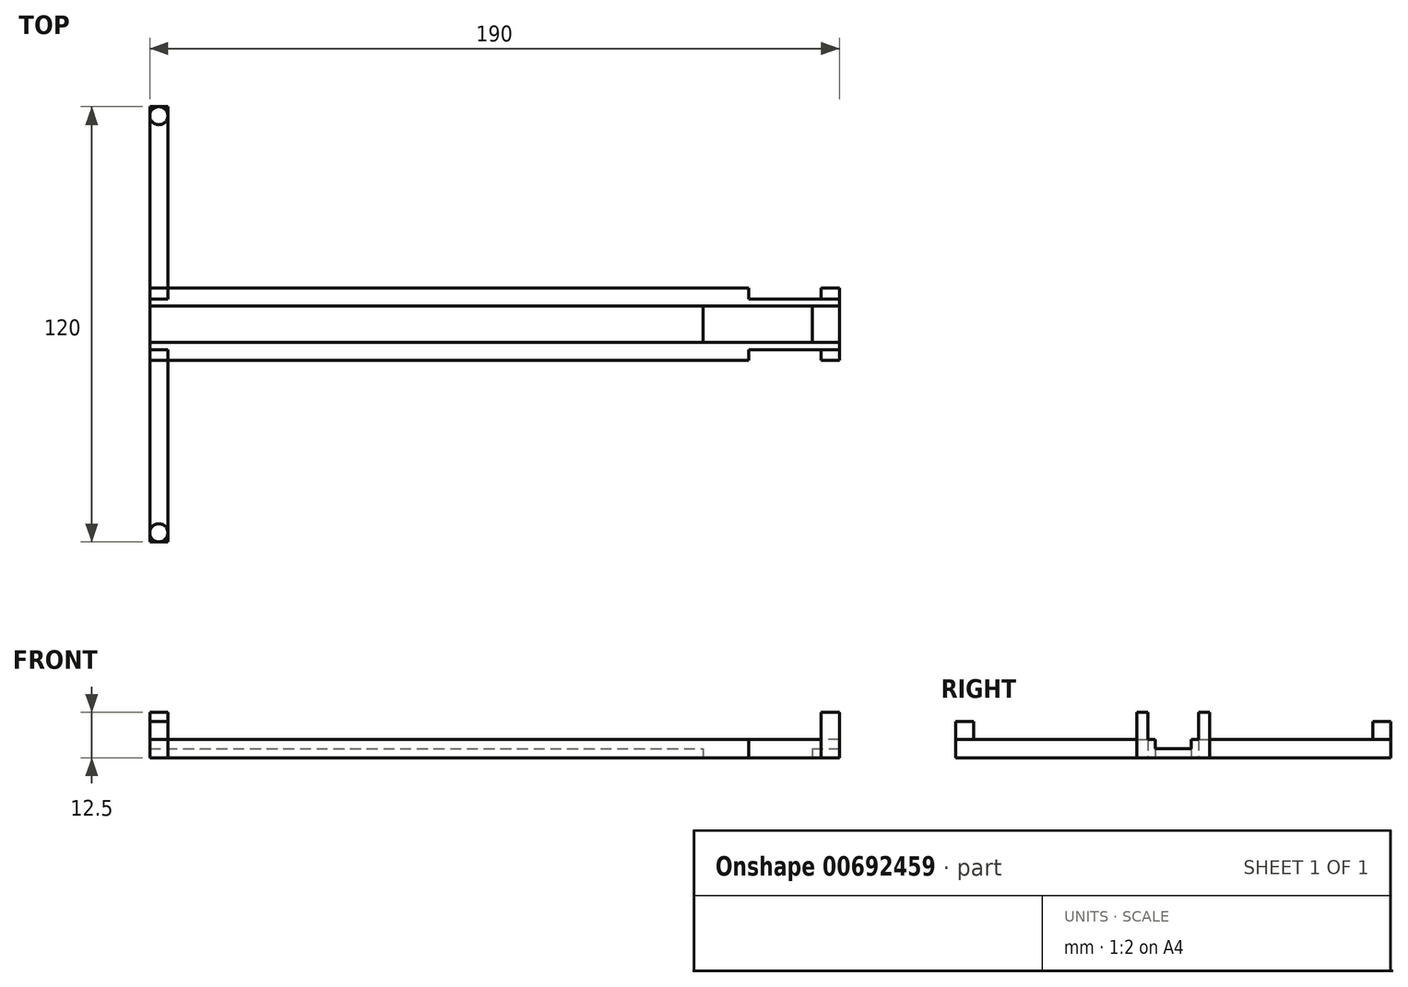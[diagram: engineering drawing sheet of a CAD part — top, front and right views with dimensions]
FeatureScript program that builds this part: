
annotation { "Feature Type Name" : "Feature", "Feature Type Description" : "" }
export const myFeature = defineFeature(function(context is Context, id is Id, definition is map)
    precondition{}
    {
        {
            var Q0;
            Q0=qCreatedBy(makeId("Top.planeOp"),FACE);
            var sketch = newSketch(context, id + "F0", { "sketchPlane" : qUnion([Q0])});
            skLineSegment(sketch, "E0", {"start": v(0, 0) * mm, "end": v(-100, 0) * mm, "construction": true});
            skLineSegment(sketch, "E1", {"start": v(0, 0) * mm, "end": v(92.5, 0) * mm, "construction": true});
            skLineSegment(sketch, "E2", {"start": v(-100, 0) * mm, "end": v(-100, -10) * mm});
            skLineSegment(sketch, "E3", {"start": v(-100, 0) * mm, "end": v(-100, 10) * mm});
            skLineSegment(sketch, "E4", {"start": v(-100, 10) * mm, "end": v(90, 10) * mm});
            skLineSegment(sketch, "E5", {"start": v(90, 10) * mm, "end": v(90, -10) * mm});
            skLineSegment(sketch, "E6", {"start": v(90, -10) * mm, "end": v(-100, -10) * mm});
            skLineSegment(sketch, "E7", {"start": v(92.5, 0) * mm, "end": v(82.5, 0) * mm});
            skLineSegment(sketch, "E8", {"start": v(82.5, 0) * mm, "end": v(52.5, 0) * mm});
            skLineSegment(sketch, "E9", {"start": v(52.5, 0) * mm, "end": v(52.5, -5) * mm});
            skLineSegment(sketch, "E10", {"start": v(52.5, 0) * mm, "end": v(52.5, 5) * mm});
            skLineSegment(sketch, "E11", {"start": v(52.5, 5) * mm, "end": v(82.5, 5) * mm});
            skLineSegment(sketch, "E12", {"start": v(82.5, 5) * mm, "end": v(82.5, -5) * mm});
            skLineSegment(sketch, "E13", {"start": v(82.5, -5) * mm, "end": v(52.5, -5) * mm});
            skLineSegment(sketch, "E14", {"start": v(90, -10) * mm, "end": v(85, -10) * mm});
            skLineSegment(sketch, "E15", {"start": v(85, -10) * mm, "end": v(85, -7) * mm});
            skLineSegment(sketch, "E16", {"start": v(85, -7) * mm, "end": v(65, -7) * mm});
            skLineSegment(sketch, "E17", {"start": v(65, -7) * mm, "end": v(65, -10) * mm});
            skLineSegment(sketch, "E18.MirrorCS", {"start": v(65, 7) * mm, "end": v(65, 10) * mm});
            skLineSegment(sketch, "E19.MirrorCS", {"start": v(85, 7) * mm, "end": v(65, 7) * mm});
            skLineSegment(sketch, "E20.MirrorCS", {"start": v(85, 10) * mm, "end": v(85, 7) * mm});
            skLineSegment(sketch, "E21", {"start": v(65, 10) * mm, "end": v(62, 10) * mm});
            skLineSegment(sketch, "E22", {"start": v(62, 10) * mm, "end": v(62, 13) * mm});
            skLineSegment(sketch, "E23", {"start": v(62, 13) * mm, "end": v(90, 13) * mm});
            skLineSegment(sketch, "E24", {"start": v(90, 13) * mm, "end": v(90, 10) * mm});
            skLineSegment(sketch, "E25", {"start": v(90, -10) * mm, "end": v(90, -13) * mm});
            skLineSegment(sketch, "E26", {"start": v(90, -13) * mm, "end": v(62, -13) * mm});
            skLineSegment(sketch, "E27", {"start": v(62, -13) * mm, "end": v(62, -10) * mm});
            skSolve(sketch);
        }
        {
            var Q0;
            {var subQ3=sQuery(id+"F0.wireOp",EDGE,"E2");Q0=makeQuery(id+"F0.imprint","IMPRINT",FACE,{"disambiguationData":[TD([[makeQuery(id+"F0.imprint","IMPRINT",EDGE,{"derivedFrom":subQ3}),1.0]])]});}
            var Q1;
            {var subQ1=sQuery(id+"F0.wireOp",EDGE,"E7");Q1=makeQuery(id+"F0.imprint","IMPRINT",FACE,{"disambiguationData":[TD([[makeQuery(id+"F0.imprint","IMPRINT",EDGE,{"derivedFrom":subQ1}),1.0]])]});}
            var Q2;
            Q2=makeQuery(id+"F0.imprint","IMPRINT",FACE,{"disambiguationData":[TD([[makeQuery(id+"F0.imprint","IMPRINT",EDGE,{"derivedFrom":sQuery(id+"F0.wireOp",EDGE,"4Cq9GJmo-zFON-n53V-LNe4-NIe40CGE9Hls")}),-1.0]])]});
            var Q3;
            {var subQ0=sQuery(id+"F0.wireOp",EDGE,"4db24e6f-349c-45e0-a969-8d08b926a6950.MirrorCS");Q3=makeQuery(id+"F0.imprint","IMPRINT",FACE,{"disambiguationData":[TD([[makeQuery(id+"F0.imprint","IMPRINT",EDGE,{"derivedFrom":subQ0}),1.0]])]});}
            var Q4;
            {var subQ0=sQuery(id+"F0.wireOp",EDGE,"E14");Q4=makeQuery(id+"F0.imprint","IMPRINT",FACE,{"disambiguationData":[TD([[makeQuery(id+"F0.imprint","IMPRINT",EDGE,{"derivedFrom":subQ0}),1.0]])]});}
            var Q5;
            {var subQ0=sQuery(id+"F0.wireOp",EDGE,"E21");Q5=makeQuery(id+"F0.imprint","IMPRINT",FACE,{"disambiguationData":[TD([[makeQuery(id+"F0.imprint","IMPRINT",EDGE,{"derivedFrom":subQ0}),-1.0]])]});}
            extrude(context, id + "F1", {"entities" : qUnion([Q0, Q1, Q2, Q3, Q4, Q5]), "depth" : 5 * mm, "offsetDistance" : 25 * mm});
        }
        {
            var Q0;
            Q0=makeQuery(id+"F1.opExtrude","SWEPT_FACE",FACE,{"disambiguationData":[OSD([sQuery(id+"F0.wireOp",EDGE,"E5")])]});
            var sketch = newSketch(context, id + "F2", { "sketchPlane" : qUnion([Q0])});
            skLineSegment(sketch, "E28", {"start": v(-10, 5) * mm, "end": v(-5, 5) * mm});
            skLineSegment(sketch, "E29", {"start": v(10, 5) * mm, "end": v(5, 5) * mm});
            skPoint(sketch, "E30.endSnap0", {"position": v(-10, 2.5) * mm});
            skLineSegment(sketch, "E31", {"start": v(-5, 5) * mm, "end": v(-5, 2.5) * mm});
            skLineSegment(sketch, "E32", {"start": v(-5, 2.5) * mm, "end": v(5, 2.5) * mm});
            skLineSegment(sketch, "E33", {"start": v(5, 2.5) * mm, "end": v(5, 5) * mm});
            skSolve(sketch);
        }
        {
            var Q0;
            {var subQ0=sQuery(id+"F2.wireOp",EDGE,"E30");Q0=makeQuery(id+"F2.imprint","IMPRINT",FACE,{"disambiguationData":[TD([[makeQuery(id+"F2.imprint","IMPRINT",EDGE,{"derivedFrom":subQ0}),1.0]])]});}
            var Q1;
            {var subQ0=sQuery(id+"F2.wireOp",EDGE,"E31");Q1=makeQuery(id+"F2.imprint","IMPRINT",FACE,{"disambiguationData":[TD([[makeQuery(id+"F2.imprint","IMPRINT",EDGE,{"derivedFrom":subQ0}),1.0]])]});}
            extrude(context, id + "F3", {"entities" : qUnion([Q0, Q1]), "operationType" : NewBodyOperationType.REMOVE, "oppositeDirection" : true, "depth" : 200 * mm, "offsetDistance" : 25 * mm});
        }
        {
            var Q0;
            {var subQ0=sQuery(id+"F0.wireOp",EDGE,"E3");var subQ1=sQuery(id+"F0.wireOp",EDGE,"E2");var subQ2=sQuery(id+"F0.wireOp",EDGE,"E4");var subQ3=sQuery(id+"F0.wireOp",EDGE,"E5");Q0=makeQuery(id+"F3.boolean.opBoolean","SPLIT",FACE,{"disambiguationData":[TD([makeQuery(id+"F1.opExtrude","SWEPT_FACE",FACE,{"disambiguationData":[OSD([subQ2])]})])],"derivedFrom":makeQuery(id+"F1.opExtrude","CAP_FACE",FACE,{"disambiguationData":[OSD([subQ1,subQ0,subQ2,subQ3,sQuery(id+"F0.wireOp",EDGE,"E6")])],"isStart":false})});}
            var sketch = newSketch(context, id + "F4", { "sketchPlane" : qUnion([Q0])});
            skLineSegment(sketch, "E34", {"start": v(-100, 10) * mm, "end": v(-100, -10) * mm});
            skLineSegment(sketch, "E35", {"start": v(-100, 7) * mm, "end": v(-95, 7) * mm});
            skLineSegment(sketch, "E36", {"start": v(-95, 7) * mm, "end": v(-95, 10) * mm});
            skLineSegment(sketch, "E37", {"start": v(-100, -10) * mm, "end": v(-95, -10) * mm});
            skLineSegment(sketch, "E38", {"start": v(-95, -10) * mm, "end": v(-95, -7) * mm});
            skLineSegment(sketch, "E39", {"start": v(-95, -7) * mm, "end": v(-100, -7) * mm});
            skLineSegment(sketch, "E40", {"start": v(-100, 10) * mm, "end": v(-5, 10) * mm});
            skLineSegment(sketch, "E41", {"start": v(-5, 10) * mm, "end": v(-5, -10) * mm});
            skLineSegment(sketch, "E42.MirrorCS", {"start": v(85, -7) * mm, "end": v(90, -7) * mm});
            skLineSegment(sketch, "E43.MirrorCS", {"start": v(85, -10) * mm, "end": v(85, -7) * mm});
            skLineSegment(sketch, "E44.MirrorCS", {"start": v(85, 7) * mm, "end": v(85, 10) * mm});
            skLineSegment(sketch, "E45.MirrorCS", {"start": v(90, 7) * mm, "end": v(85, 7) * mm});
            skLineSegment(sketch, "E46", {"start": v(85, -10) * mm, "end": v(90, -10) * mm});
            skLineSegment(sketch, "E47", {"start": v(90, -10) * mm, "end": v(90, -7) * mm});
            skLineSegment(sketch, "E48", {"start": v(85, 10) * mm, "end": v(90, 10) * mm});
            skLineSegment(sketch, "E49", {"start": v(90, 10) * mm, "end": v(90, 7) * mm});
            skLineSegment(sketch, "E50", {"start": v(-100, 7) * mm, "end": v(-100, -7) * mm});
            skSolve(sketch);
        }
        {
            var Q0;
            Q0 = qSketchRegion(id + "F4", true);
            var Q1;
            {var subQ0=sQuery(id+"F4.wireOp",EDGE,"E35");Q1=makeQuery(id+"F4.imprint","IMPRINT",FACE,{"disambiguationData":[TD([[makeQuery(id+"F4.imprint","IMPRINT",EDGE,{"derivedFrom":subQ0}),1.0]])]});}
            extrude(context, id + "F5", {"entities" : qUnion([Q0, Q1]), "operationType" : NewBodyOperationType.ADD, "depth" : 7.5 * mm, "offsetDistance" : 25 * mm});
        }
        {
            var Q0;
            Q0=makeQuery(id+"F5.boolean.opBoolean","MERGE",FACE,{"derivedFrom":[makeQuery(id+"F1.opExtrude","SWEPT_FACE",FACE,{"disambiguationData":[OSD([sQuery(id+"F0.wireOp",EDGE,"E6")])]}),makeQuery(id+"F5.opExtrude","SWEPT_FACE",FACE,{"disambiguationData":[OSD([sQuery(id+"F4.wireOp",EDGE,"E37")])]}),makeQuery(id+"F5.opExtrude","SWEPT_FACE",FACE,{"disambiguationData":[OSD([sQuery(id+"F4.wireOp",EDGE,"KvMu5L7A-9GDo-6Ov3-ij6E-cGlpLKPQahlB")])]})]});
            var sketch = newSketch(context, id + "F6", { "sketchPlane" : qUnion([Q0])});
            skLineSegment(sketch, "E51", {"start": v(-100, 0) * mm, "end": v(-95, 0) * mm});
            skLineSegment(sketch, "E52", {"start": v(-95, 0) * mm, "end": v(-95, 5) * mm});
            skLineSegment(sketch, "E53", {"start": v(-95, 5) * mm, "end": v(-100, 5) * mm});
            skSolve(sketch);
        }
        {
            var Q0;
            {var subQ0=sQuery(id+"F6.wireOp",EDGE,"E51");Q0=makeQuery(id+"F6.imprint","IMPRINT",FACE,{"disambiguationData":[TD([[makeQuery(id+"F6.imprint","IMPRINT",EDGE,{"derivedFrom":subQ0}),-1.0]])]});}
            extrude(context, id + "F7", {"entities" : qUnion([Q0]), "operationType" : NewBodyOperationType.ADD, "depth" : 50 * mm, "offsetDistance" : 25 * mm});
        }
        {
            var Q0;
            {var subQ0=sQuery(id+"F0.wireOp",EDGE,"E4");Q0=makeQuery(id+"F5.boolean.opBoolean","MERGE",FACE,{"derivedFrom":[makeQuery(id+"F1.opExtrude","SWEPT_FACE",FACE,{"disambiguationData":[OSD([subQ0])]}),makeQuery(id+"F5.opExtrude","SWEPT_FACE",FACE,{"disambiguationData":[OSD([sQuery(id+"F4.wireOp",EDGE,"chlLDGLh-5rKh-LiF5-0Xwm-xtgiCiL9NvXN")])]}),makeQuery(id+"F5.opExtrude","SWEPT_FACE",FACE,{"disambiguationData":[OSD([subQ0])]})]});}
            var sketch = newSketch(context, id + "F8", { "sketchPlane" : qUnion([Q0])});
            skLineSegment(sketch, "E54.bottom", {"start": v(100, 0) * mm, "end": v(95, 0) * mm});
            skLineSegment(sketch, "E54.top", {"start": v(100, 5) * mm, "end": v(95, 5) * mm});
            skLineSegment(sketch, "E54.left", {"start": v(100, 0) * mm, "end": v(100, 5) * mm});
            skLineSegment(sketch, "E54.right", {"start": v(95, 0) * mm, "end": v(95, 5) * mm});
            skSolve(sketch);
        }
        {
            var Q0;
            Q0=makeQuery(id+"F8.imprint","IMPRINT",FACE,{"disambiguationData":[TD([[makeQuery(id+"F8.imprint","IMPRINT",EDGE,{"derivedFrom":sQuery(id+"F8.wireOp",EDGE,"E54.bottom")}),-1.0]])]});
            extrude(context, id + "F9", {"entities" : qUnion([Q0]), "operationType" : NewBodyOperationType.ADD, "depth" : 50 * mm, "offsetDistance" : 25 * mm});
        }
        {
            var Q0;
            Q0=makeQuery(id+"F7.opExtrude","SWEPT_FACE",FACE,{"disambiguationData":[OSD([sQuery(id+"F6.wireOp",EDGE,"E53")])]});
            var sketch = newSketch(context, id + "F10", { "sketchPlane" : qUnion([Q0])});
            skLineSegment(sketch, "E55", {"start": v(-97.5, -60) * mm, "end": v(-97.5, -57.5) * mm});
            skCircle(sketch, "E56", {"center": v(-97.5, -57.5) * mm, "radius": 2.5 * mm});
            skSolve(sketch);
        }
        {
            var Q0;
            Q0=makeQuery(id+"F9.opExtrude","SWEPT_FACE",FACE,{"disambiguationData":[OSD([sQuery(id+"F8.wireOp",EDGE,"E54.top")])]});
            var sketch = newSketch(context, id + "F11", { "sketchPlane" : qUnion([Q0])});
            skLineSegment(sketch, "E57", {"start": v(-97.5, 60) * mm, "end": v(-97.5, 57.5) * mm});
            skCircle(sketch, "E58", {"center": v(-97.5, 57.5) * mm, "radius": 2.5 * mm});
            skSolve(sketch);
        }
        {
            var Q0;
            {var subQ0=sQuery(id+"F10.wireOp",EDGE,"E56");var subQ1=sQuery(id+"F6.wireOp",EDGE,"E53");var subQ6=makeQuery(id+"F10.imprint","INTERSECT",VERTEX,{"derivedFrom":[makeQuery(id+"F7.opExtrude","CAP_EDGE",EDGE,{"disambiguationData":[OSD([subQ1])],"isStart":false}),subQ0]});Q0=makeQuery(id+"F10.imprint","IMPRINT",FACE,{"disambiguationData":[TD([[makeQuery(id+"F10.imprint","IMPRINT",EDGE,{"disambiguationData":[TD([[subQ6,1.0]])],"derivedFrom":subQ0}),1.0]])]});}
            var Q1;
            {var subQ0=sQuery(id+"F11.wireOp",EDGE,"E58");var subQ1=sQuery(id+"F8.wireOp",EDGE,"E54.top");var subQ2=makeQuery(id+"F11.imprint","INTERSECT",VERTEX,{"derivedFrom":[makeQuery(id+"F9.opExtrude","CAP_EDGE",EDGE,{"disambiguationData":[OSD([subQ1])],"isStart":false}),subQ0]});Q1=makeQuery(id+"F11.imprint","IMPRINT",FACE,{"disambiguationData":[TD([[makeQuery(id+"F11.imprint","IMPRINT",EDGE,{"disambiguationData":[TD([[subQ2,1.0]])],"derivedFrom":subQ0}),1.0]])]});}
            extrude(context, id + "F12", {"entities" : qUnion([Q0, Q1]), "operationType" : NewBodyOperationType.ADD, "depth" : 5 * mm, "offsetDistance" : 25 * mm});
        }
    });
